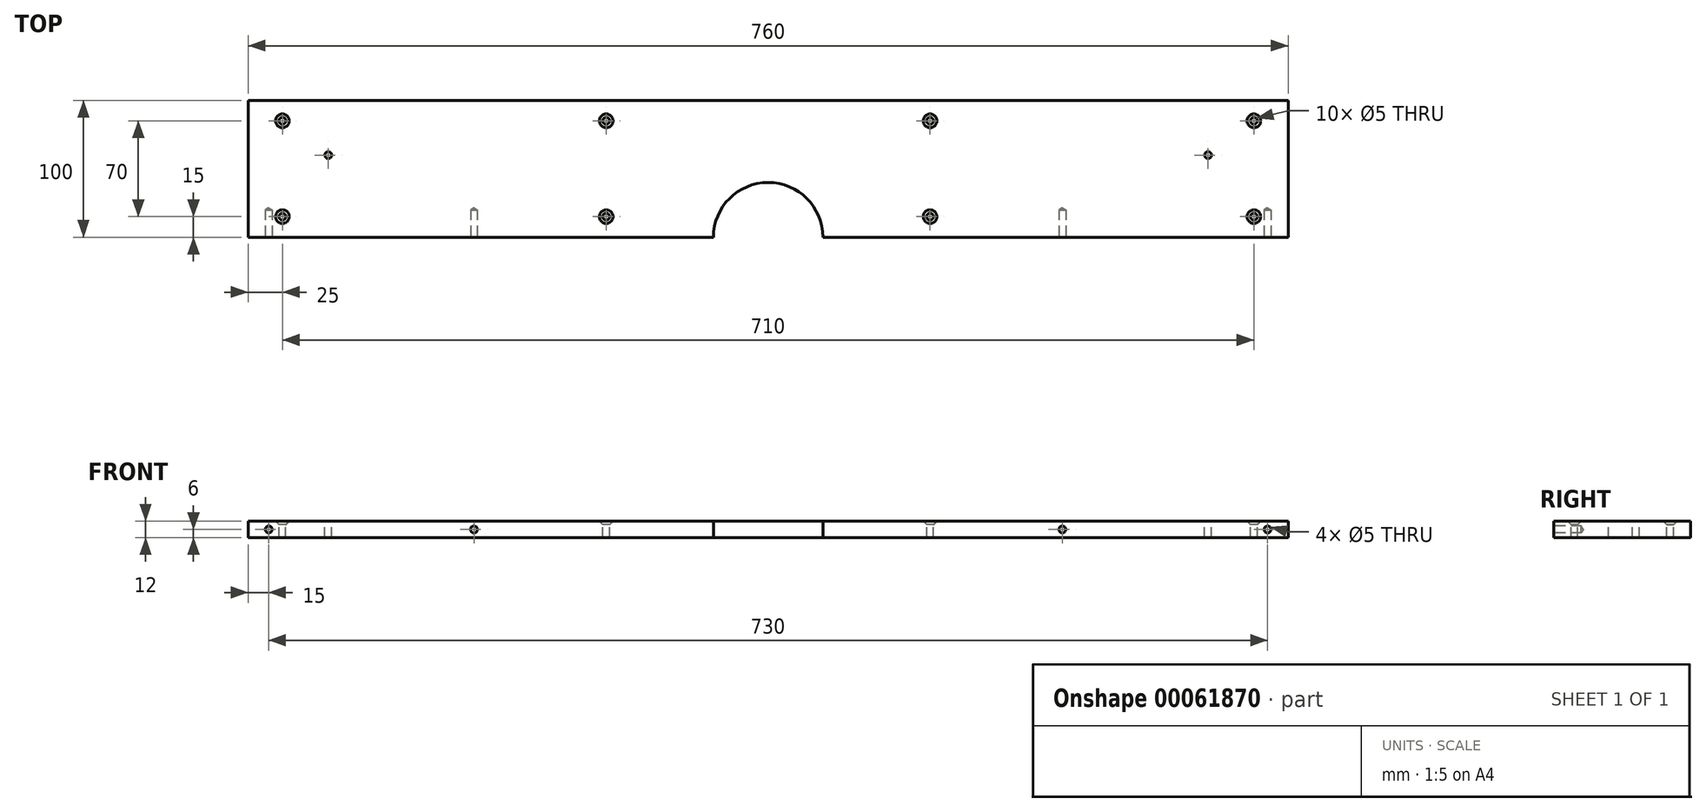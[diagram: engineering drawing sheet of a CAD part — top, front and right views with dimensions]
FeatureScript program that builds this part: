
annotation { "Feature Type Name" : "Feature", "Feature Type Description" : "" }
export const myFeature = defineFeature(function(context is Context, id is Id, definition is map)
    precondition{}
    {
        {
            var Q0;
            Q0=qCreatedBy(makeId("Top.planeOp"),FACE);
            var sketch = newSketch(context, id + "F0", { "sketchPlane" : qUnion([Q0])});
            skLineSegment(sketch, "E0.bottom", {"start": v(0, 0) * mm, "end": v(760, 0) * mm});
            skLineSegment(sketch, "E0.top", {"start": v(0, 100) * mm, "end": v(760, 100) * mm});
            skLineSegment(sketch, "E0.left", {"start": v(0, 0) * mm, "end": v(0, 100) * mm});
            skLineSegment(sketch, "E0.right", {"start": v(760, 0) * mm, "end": v(760, 100) * mm});
            skSolve(sketch);
        }
        {
            var Q0;
            Q0=makeQuery(id+"F0.imprint","IMPRINT",FACE,{"disambiguationData":[TD([[makeQuery(id+"F0.imprint","IMPRINT",EDGE,{"derivedFrom":sQuery(id+"F0.wireOp",EDGE,"E0.bottom")}),1.0]])]});
            extrude(context, id + "F1", {"entities" : qUnion([Q0]), "depth" : 12 * mm});
        }
        {
            var Q0;
            Q0=makeQuery(id+"F1.opExtrude","CAP_FACE",FACE,{"disambiguationData":[OSD([sQuery(id+"F0.wireOp",EDGE,"E0.bottom"),sQuery(id+"F0.wireOp",EDGE,"E0.top"),sQuery(id+"F0.wireOp",EDGE,"E0.left"),sQuery(id+"F0.wireOp",EDGE,"E0.right")])],"isStart":false});
            var sketch = newSketch(context, id + "F2", { "sketchPlane" : qUnion([Q0])});
            skPoint(sketch, "E1", {"position": v(58.5, 60) * mm});
            skPoint(sketch, "E2", {"position": v(701.5, 60) * mm});
            skLineSegment(sketch, "E3", {"start": v(50, 100) * mm, "end": v(50, 0) * mm, "construction": true});
            skLineSegment(sketch, "E4", {"start": v(710, 100) * mm, "end": v(710, 0) * mm, "construction": true});
            skSolve(sketch);
        }
        {
            var Q0;
            Q0=sQuery(id+"F2.wireOp",VERTEX,"E1");
            var Q1;
            Q1=sQuery(id+"F2.wireOp",VERTEX,"E2");
            var Q2;
            Q2=makeQuery(id+"F1.opExtrude","SWEPT_BODY",BODY,{"disambiguationData":[OSD([sQuery(id+"F0.wireOp",EDGE,"E0.bottom"),sQuery(id+"F0.wireOp",EDGE,"E0.top"),sQuery(id+"F0.wireOp",EDGE,"E0.left"),sQuery(id+"F0.wireOp",EDGE,"E0.right")])]});
            hole(context, id + "F3", {"style" : HoleStyle.SIMPLE, "holeDiameter" : 5 * mm, "endStyle" : HoleEndStyle.THROUGH, "locations" : qUnion([Q0, Q1]), "scope" : qUnion([Q2])});
        }
        {
            var Q0;
            Q0=makeQuery(id+"F1.opExtrude","CAP_FACE",FACE,{"disambiguationData":[OSD([sQuery(id+"F0.wireOp",EDGE,"E0.bottom"),sQuery(id+"F0.wireOp",EDGE,"E0.top"),sQuery(id+"F0.wireOp",EDGE,"E0.left"),sQuery(id+"F0.wireOp",EDGE,"E0.right")])],"isStart":false});
            var sketch = newSketch(context, id + "F4", { "sketchPlane" : qUnion([Q0])});
            skCircle(sketch, "E5", {"center": v(380, 0) * mm, "radius": 40 * mm});
            skSolve(sketch);
        }
        {
            var Q0;
            Q0 = qSketchRegion(id + "F4", true);
            extrude(context, id + "F5", {"entities" : qUnion([Q0]), "operationType" : NewBodyOperationType.REMOVE, "oppositeDirection" : true, "depth" : 25 * mm});
        }
        {
            var Q0;
            {var subQ1=sQuery(id+"F0.wireOp",EDGE,"E0.left");var subQ3=sQuery(id+"F0.wireOp",EDGE,"E0.bottom");Q0=makeQuery(id+"F5.boolean.opBoolean","SPLIT",FACE,{"disambiguationData":[TD([makeQuery(id+"F1.opExtrude","SWEPT_FACE",FACE,{"disambiguationData":[OSD([subQ1])]})])],"derivedFrom":makeQuery(id+"F1.opExtrude","SWEPT_FACE",FACE,{"disambiguationData":[OSD([subQ3])]})});}
            var sketch = newSketch(context, id + "F6", { "sketchPlane" : qUnion([Q0])});
            skLineSegment(sketch, "E6", {"start": v(0, 6) * mm, "end": v(15, 6) * mm, "construction": true});
            skLineSegment(sketch, "E7", {"start": v(15, 6) * mm, "end": v(165, 6) * mm, "construction": true});
            skSolve(sketch);
        }
        {
            var Q0;
            {var subQ0=sQuery(id+"F0.wireOp",EDGE,"E0.right");var subQ3=sQuery(id+"F0.wireOp",EDGE,"E0.bottom");Q0=makeQuery(id+"F5.boolean.opBoolean","SPLIT",FACE,{"disambiguationData":[TD([makeQuery(id+"F1.opExtrude","SWEPT_FACE",FACE,{"disambiguationData":[OSD([subQ0])]})])],"derivedFrom":makeQuery(id+"F1.opExtrude","SWEPT_FACE",FACE,{"disambiguationData":[OSD([subQ3])]})});}
            var sketch = newSketch(context, id + "F7", { "sketchPlane" : qUnion([Q0])});
            skLineSegment(sketch, "E8", {"start": v(760, 6) * mm, "end": v(745, 6) * mm, "construction": true});
            skLineSegment(sketch, "E9", {"start": v(745, 6) * mm, "end": v(595, 6) * mm, "construction": true});
            skSolve(sketch);
        }
        {
            var Q0;
            Q0=sQuery(id+"F6.wireOp",VERTEX,"E6.end");
            var Q1;
            Q1=sQuery(id+"F6.wireOp",VERTEX,"E7.end");
            var Q2;
            Q2=sQuery(id+"F7.wireOp",VERTEX,"E9.end");
            var Q3;
            Q3=sQuery(id+"F7.wireOp",VERTEX,"E9.start");
            var Q4;
            Q4=makeQuery(id+"F1.opExtrude","SWEPT_BODY",BODY,{"disambiguationData":[OSD([sQuery(id+"F0.wireOp",EDGE,"E0.bottom"),sQuery(id+"F0.wireOp",EDGE,"E0.top"),sQuery(id+"F0.wireOp",EDGE,"E0.left"),sQuery(id+"F0.wireOp",EDGE,"E0.right")])]});
            hole(context, id + "F8", {"style" : HoleStyle.SIMPLE, "holeDiameter" : 5 * mm, "endStyle" : HoleEndStyle.BLIND, "holeDepth" : 20 * mm, "locations" : qUnion([Q0, Q1, Q2, Q3]), "scope" : qUnion([Q4])});
        }
        {
            var Q0;
            Q0=makeQuery(id+"F1.opExtrude","CAP_FACE",FACE,{"disambiguationData":[OSD([sQuery(id+"F0.wireOp",EDGE,"E0.bottom"),sQuery(id+"F0.wireOp",EDGE,"E0.top"),sQuery(id+"F0.wireOp",EDGE,"E0.left"),sQuery(id+"F0.wireOp",EDGE,"E0.right")])],"isStart":false});
            var sketch = newSketch(context, id + "F9", { "sketchPlane" : qUnion([Q0])});
            skLineSegment(sketch, "E10", {"start": v(25, 0) * mm, "end": v(25, 100) * mm, "construction": true});
            skPoint(sketch, "E11", {"position": v(25, 15) * mm});
            skPoint(sketch, "E12.0.1.0", {"position": v(25, 85) * mm});
            skPoint(sketch, "E12.1.0.0", {"position": v(261.67, 15) * mm});
            skPoint(sketch, "E12.1.1.0", {"position": v(261.67, 85) * mm});
            skPoint(sketch, "E12.2.0.0", {"position": v(498.33, 15) * mm});
            skPoint(sketch, "E12.2.1.0", {"position": v(498.33, 85) * mm});
            skPoint(sketch, "E12.3.0.0", {"position": v(735, 15) * mm});
            skPoint(sketch, "E12.3.1.0", {"position": v(735, 85) * mm});
            skLineSegment(sketch, "E12.direction1", {"start": v(25, 15) * mm, "end": v(261.67, 15) * mm, "construction": true});
            skLineSegment(sketch, "E12.direction2", {"start": v(25, 15) * mm, "end": v(25, 85) * mm, "construction": true});
            skSolve(sketch);
        }
        {
            var Q0;
            Q0=sQuery(id+"F9.wireOp",VERTEX,"E11");
            var Q1;
            Q1=sQuery(id+"F9.wireOp",VERTEX,"E12.0.1.0");
            var Q2;
            Q2=sQuery(id+"F9.wireOp",VERTEX,"E12.1.0.0");
            var Q3;
            Q3=sQuery(id+"F9.wireOp",VERTEX,"E12.1.1.0");
            var Q4;
            Q4=sQuery(id+"F9.wireOp",VERTEX,"E12.2.0.0");
            var Q5;
            Q5=sQuery(id+"F9.wireOp",VERTEX,"E12.2.1.0");
            var Q6;
            Q6=sQuery(id+"F9.wireOp",VERTEX,"E12.3.1.0");
            var Q7;
            Q7=sQuery(id+"F9.wireOp",VERTEX,"E12.3.0.0");
            var Q8;
            Q8=makeQuery(id+"F1.opExtrude","SWEPT_BODY",BODY,{"disambiguationData":[OSD([sQuery(id+"F0.wireOp",EDGE,"E0.bottom"),sQuery(id+"F0.wireOp",EDGE,"E0.top"),sQuery(id+"F0.wireOp",EDGE,"E0.left"),sQuery(id+"F0.wireOp",EDGE,"E0.right")])]});
            hole(context, id + "F10", {"style" : HoleStyle.C_SINK, "holeDiameter" : 5 * mm, "cSinkDiameter" : 10 * mm, "endStyle" : HoleEndStyle.THROUGH, "locations" : qUnion([Q0, Q1, Q2, Q3, Q4, Q5, Q6, Q7]), "scope" : qUnion([Q8]), "cSinkAngle" : 90 * degree});
        }
    });
